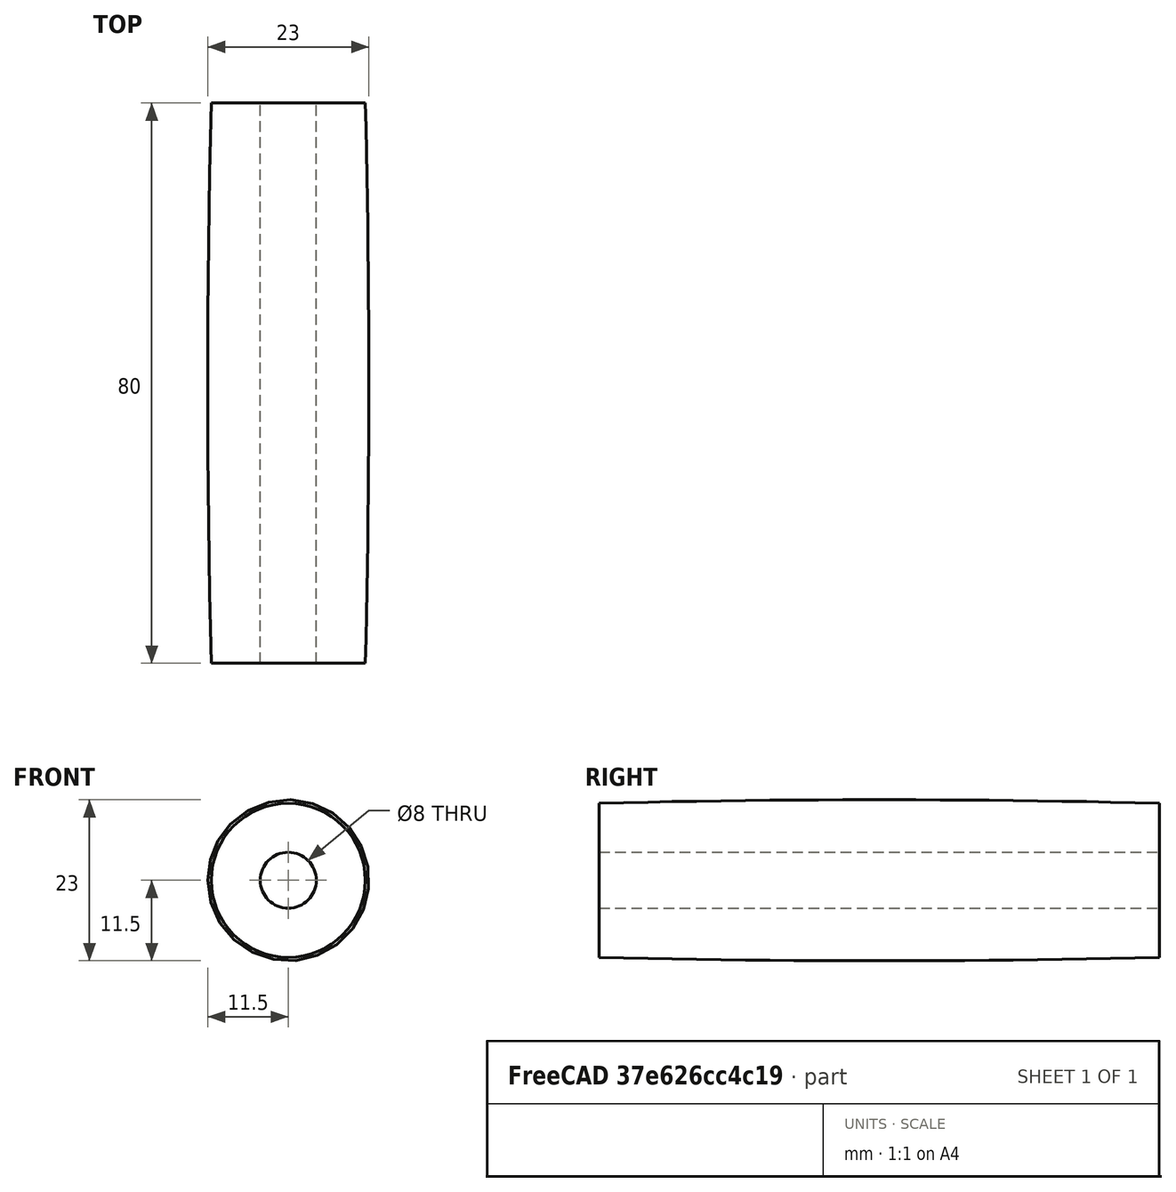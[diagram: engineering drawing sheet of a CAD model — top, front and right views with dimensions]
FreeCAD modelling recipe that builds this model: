
FCSTD DOCUMENT  (FreeCAD 0.17R13509 (Git))
Label: roller
License: All rights reserved
LicenseURL: http://en.wikipedia.org/wiki/All_rights_reserved
objects: Sketcher::SketchObject×1, PartDesign::Revolution×1
note: 3 computed .brp shape members not serialized (recipe doc carries the construction recipe); baked Part::Feature solids carry a one-line shape summary decoded from their .brp

FEATURE [Sketcher::SketchObject] Sketch023
  MapMode = 5
  Placement = pos=(0,36,-100) rot=(0,0,1;1.5708rad)
  sketch-geometry (5):
    g0: LineSegment StartX=-40 StartY=4 StartZ=0 EndX=40 EndY=4 EndZ=0
    g1: LineSegment StartX=-40 StartY=4 StartZ=0 EndX=-40 EndY=11 EndZ=0
    g2: LineSegment StartX=40 StartY=4 StartZ=0 EndX=40 EndY=11 EndZ=0
    g3: GeomPoint [constr] X=0 Y=11.5 Z=0
    g4: ArcOfCircle CenterX=0 CenterY=-1588.75 CenterZ=0 NormalX=0 NormalY=0 NormalZ=1 AngleXU=0 Radius=1600.25 StartAngle=1.5458 EndAngle=1.5958
  constraints (13):
    c: Horizontal(g0)
    c: Coincident(g1,g0)
    c: Vertical(g1)
    c: Coincident(g2,g0)
    c: Vertical(g2)
    c: Symmetric(g0,g0,g-2)
    c: DistanceX(g0,g0) = 80
    c: DistanceY(g0) = 4
    c: DistanceY(g2) = 11
    c: PointOnObject(g4,g-2)
    c: Coincident(g4,g1)
    c: Coincident(g4,g2)
    c: PointOnObject(g3,g4)
FEATURE [PartDesign::Revolution] Revolution001  label="Top"
  Angle = 360
  Axis = (0,1,0)
  Base = (0,36,-100)
  Placement = pos=(0,36,-100) rot=(0,0,1;1.5708rad)
  Profile = -> Sketch023
  ReferenceAxis = -> Sketch023 [H_Axis]
  Refine = true
